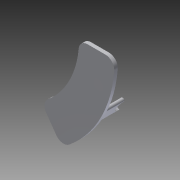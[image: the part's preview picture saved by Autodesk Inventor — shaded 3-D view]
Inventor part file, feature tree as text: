
AUTODESK INVENTOR PART (.ipt)
format: ipt  version: 2014 (Build 180170000, 170)  size: 162,816 bytes
history: native  units: mm
features: extrude x4, sketch x4, projected_geometry x3, fillet x1
ambient origin geometry x8: Origin, YZ Plane, XZ Plane, XY Plane, X Axis, Y Axis, Z Axis, Center Point
bodies: Solid1 (feature_tree)
feature tree (12):
  extrude  "Extrusion1"  Depth=100.0mm
  extrude  "Extrusion2"  Depth=50.0mm
  extrude  "Extrusion3"  Depth=5.0mm
  extrude  "Extrusion4"  Depth=5.0mm
  fillet  "Fillet1"  Radius=2.0mm
  sketch  "Sketch1"  dims[d0=100.0mm d1=100.0mm]
  sketch  "Sketch2"  dims[d2=9.599311mm d3=50.0mm]
  projected_geometry  "Projected Loop1"
  sketch  "Sketch3"  dims[d4=70.0mm d5=5.0mm]
  sketch  "Sketch4"  dims[d6=5.0mm d7=5.0mm d8=2.0mm d9=0.0mm d10=4.799655mm d12=4.0mm d15=10.0mm d16=0.0mm d17=6.0mm d18=0.5mm d19=20.0mm d20=0.0mm d21=2.0mm d22=16.0mm d23=10.0mm d24=0.0mm d25=1.0mm]
  projected_geometry  "Projected Loop2"
  projected_geometry  "Projected Loop3"
